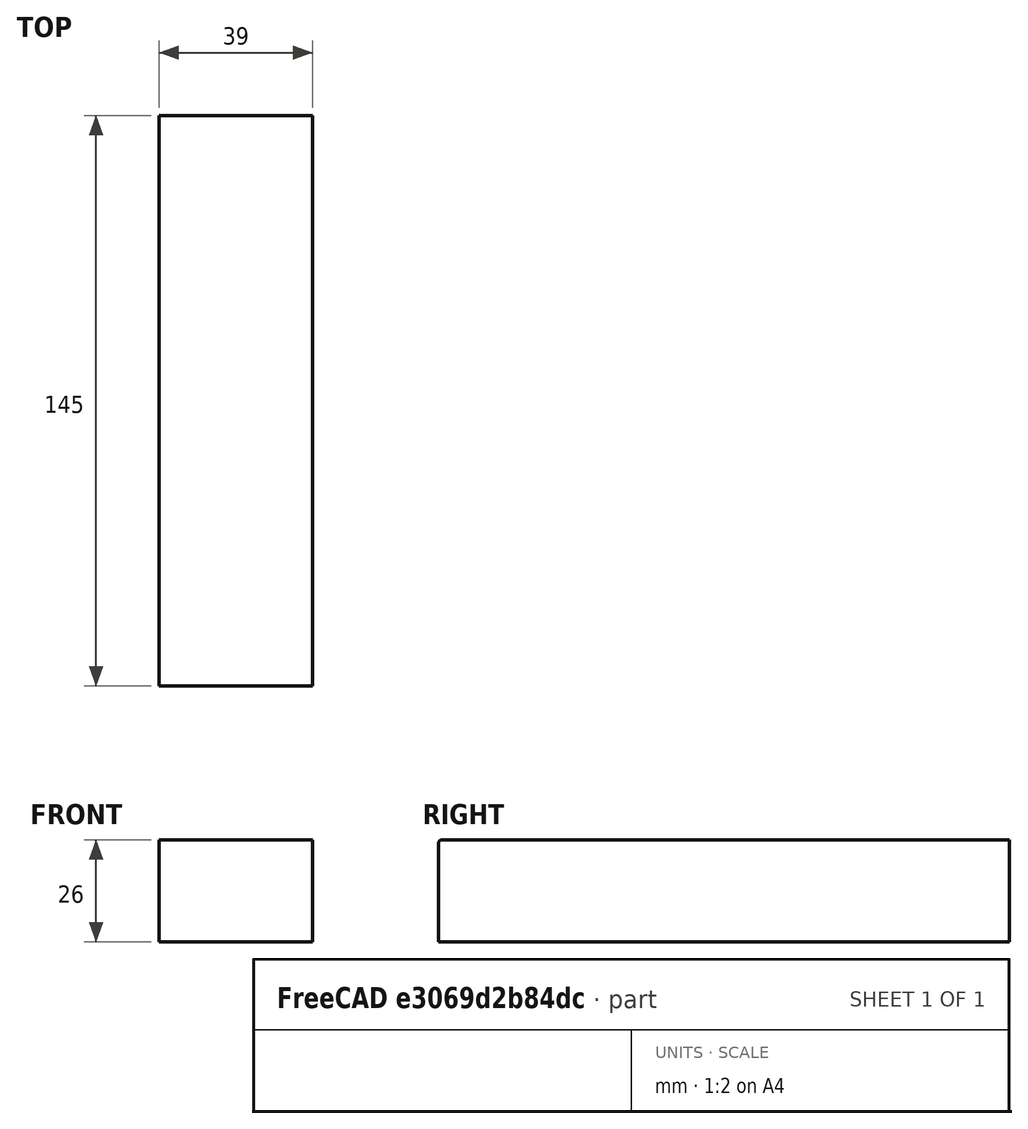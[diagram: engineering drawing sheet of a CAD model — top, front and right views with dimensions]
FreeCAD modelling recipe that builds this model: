
FCSTD DOCUMENT  (FreeCAD 0.17R13522 (Git))
Label: BlocLateralDroitClavier
License: All rights reserved
LicenseURL: http://en.wikipedia.org/wiki/All_rights_reserved
objects: Drawing::FeatureViewPython×6, Drawing::FeatureViewPart×3, Part::Box×1, Part::Fillet×1, Drawing::FeaturePage×1
note: 2 computed .brp shape members not serialized (recipe doc carries the construction recipe); baked Part::Feature solids carry a one-line shape summary decoded from their .brp

FEATURE [Part::Box] Box  label="Cube"
  AttacherType = Attacher::AttachEngine3D
  Height = 26
  Length = 39
  Width = 145
FEATURE [Part::Fillet] Fillet
  Base = -> Box
  Edges = 1 edges r=1: [Edge10]
FEATURE [Drawing::FeatureViewPart] Ortho  label="Ortho_0_0"
  Direction = (0,0,1)
  HiddenWidth = 0.15
  LineWidth = 0.35
  Rotation = 90
  ShowHiddenLines = false
  ShowSmoothLines = true
  Source = -> Fillet
  Tolerance = 0.05
  ViewResult = <g id="Ortho_0_0"\n   transform="rotate(90,108,37.6667) translate(108,37.6667) scale(1,1)"\n  >\n<g   fill="none"\n   stroke="rgb(0, 0, 0)"\n   stroke-linecap="butt"\n   stroke-linejoin="miter"\n   stroke-width="0.350000"\n   transform="scale(1,-1)"\n  >\n<path d="M0,-2.22045e-16 C0,0.00209593 0,0.00419186 0,0.00628779  C0,0.0125492 0,0.0188107 0,0.0250721  C0,0.0354203 0,0.0457685 0,0.0561167  C0,0.0704215 0,0.0847263 0,0.0990311  C0,0.117113 0,0.135194 0,0.153276  C0,0.174907 0,0.196538 0,0.218169  C0,0.243077 0,0.267985 0,0.292893  C0,0.320766 0,0.348638 0,0.37651  C0,0.436231 0,0.499433 0,0.566116  C0,0.701837 0,0.850207 0,1 " /><path id= "2" d=" M 0 1 L 0 145 " />\n<path id= "3" d=" M 0 -2.22045e-16 L 39 -2.22045e-16 " />\n<path d="M39,-2.22045e-16 C39,0.00209593 39,0.00419186 39,0.00628779  C39,0.0125492 39,0.0188107 39,0.0250721  C39,0.0354203 39,0.0457685 39,0.0561167  C39,0.0704215 39,0.0847263 39,0.0990311  C39,0.117113 39,0.135194 39,0.153276  C39,0.174907 39,0.196538 39,0.218169  C39,0.243077 39,0.267985 39,0.292893  C39,0.320766 39,0.348638 39,0.37651  C39,0.436231 39,0.499433 39,0.566116  C39,0.701837 39,0.850207 39,1 " /><path id= "5" d=" M 0 145 L 39 145 " />\n<path id= "6" d=" M 39 1 L 39 145 " />\n</g>\n<g   fill="none"\n   stroke="rgb(0, 0, 0)"\n   stroke-linecap="butt"\n   stroke-linejoin="miter"\n   stroke-width="0.350000"\n   transform="scale(1,-1)"\n  >\n<path id= "1" d=" M 0 1 L 39 1 " />\n</g>\n</g>
  Visible = false
  X = 108
  Y = 37.6667
FEATURE [Drawing::FeatureViewPart] Ortho001  label="Ortho_-1_0"
  Direction = (0,1,0)
  HiddenWidth = 0.15
  LineWidth = 0.35
  Rotation = 180
  ShowHiddenLines = false
  ShowSmoothLines = true
  Source = -> Fillet
  Tolerance = 0.05
  ViewResult = <g id="Ortho_-1_0"\n   transform="rotate(180,74,37.6667) translate(74,37.6667) scale(1,1)"\n  >\n<g   fill="none"\n   stroke="rgb(0, 0, 0)"\n   stroke-linecap="butt"\n   stroke-linejoin="miter"\n   stroke-width="0.350000"\n   transform="scale(1,-1)"\n  >\n<path id= "1" d=" M 0 0 L 26 0 " />\n<path id= "2" d=" M 0 0 L 0 39 " />\n<path id= "3" d=" M 26 0 L 26 39 " />\n<path id= "4" d=" M 0 39 L 26 39 " />\n</g>\n</g>
  Visible = false
  X = 74
  Y = 37.6667
FEATURE [Drawing::FeatureViewPart] Ortho002  label="Ortho_0_-1"
  Direction = (-1,0,0)
  HiddenWidth = 0.15
  LineWidth = 0.35
  Rotation = -90
  ShowHiddenLines = false
  ShowSmoothLines = true
  Source = -> Fillet
  Tolerance = 0.05
  ViewResult = <g id="Ortho_0_-1"\n   transform="rotate(-90,108,104.333) translate(108,104.333) scale(1,1)"\n  >\n<g   fill="none"\n   stroke="rgb(0, 0, 0)"\n   stroke-linecap="butt"\n   stroke-linejoin="miter"\n   stroke-width="0.350000"\n   transform="scale(1,-1)"\n  >\n<path id= "1" d=" M 0 0 L -25 0 " />\n<path d="M-25 2.22045e-16 A1 1 0 0 1 -26 -1" /><path id= "3" d=" M 0 0 L 0 -145 " />\n<path id= "4" d=" M -26 -1 L -26 -145 " />\n<path id= "5" d=" M 0 -145 L -26 -145 " />\n</g>\n</g>
  Visible = false
  X = 108
  Y = 104.333
FEATURE [Drawing::FeatureViewPython] dim001  # drawing view (typed FeaturePython)
  Rotation = 0
  ViewResult = <g> \n  <line x1="74.000000" y1="35.666700" x2="74.000000" y2="24.000000" style="stroke:rgb(0,0,255);stroke-width:0.30" />\n<line x1="48.000000" y1="35.666700" x2="48.000000" y2="24.000000" style="stroke:rgb(0,0,255);stroke-width:0.30" />\n<line x1="74.000000" y1="25.000000" x2="48.000000" y2="25.000000" style="stroke:rgb(0,0,255);stroke-width:0.30" /> \n  <polygon points="48.000000,25.000000 51.000000,26.000000 52.000000,25.000000 51.000000,24.000000" style="fill:rgb(0,0,255);stroke:rgb(0,0,255);stroke-width:0" /><polygon points="74.000000,25.000000 71.000000,24.000000 70.000000,25.000000 71.000000,26.000000" style="fill:rgb(0,0,255);stroke:rgb(0,0,255);stroke-width:0" /> \n  <text x="61.000000" y="23.000000" font-family="Verdana" font-size="3.6" fill="rgb(0,0,255)" text-anchor="middle" transform="rotate(0.000000 61.000000,23.000000)" > 26</text> </g>
  Visible = false
  X = 0
  Y = 0
  arrowL1 = 3
  arrowL2 = 1
  arrowW = 2
  arrow_scheme = 0
  autoPlaceOffset = 2
  autoPlaceText = true
  click1_x = 61.8667
  click1_y = 25
  click2_x = 61.8667
  click2_y = 25
  comma_decimal_place = false
  dimension_line_overshoot = 1
  gap_datum_points = 2
  halfDimension_linear = false
  lineColor = rgb(0,0,255)
  strokeWidth = 0.3
  textFormat_linear = %(value)3.0f
  textRenderer_color = rgb(0,0,255)
  textRenderer_family = Verdana
  textRenderer_size = 3.6
  unit_custom_scale = 1
  unit_scheme = 0
FEATURE [Drawing::FeatureViewPython] dim002  # drawing view (typed FeaturePython)
  Rotation = 0
  ViewResult = <g> \n  <line x1="46.000000" y1="37.666700" x2="30.533333" y2="37.666700" style="stroke:rgb(0,0,255);stroke-width:0.30" />\n<line x1="46.000000" y1="76.666700" x2="30.533333" y2="76.666700" style="stroke:rgb(0,0,255);stroke-width:0.30" />\n<line x1="31.533333" y1="37.666700" x2="31.533333" y2="76.666700" style="stroke:rgb(0,0,255);stroke-width:0.30" /> \n  <polygon points="31.533333,76.666700 32.533333,73.666700 31.533333,72.666700 30.533333,73.666700" style="fill:rgb(0,0,255);stroke:rgb(0,0,255);stroke-width:0" /><polygon points="31.533333,37.666700 30.533333,40.666700 31.533333,41.666700 32.533333,40.666700" style="fill:rgb(0,0,255);stroke:rgb(0,0,255);stroke-width:0" /> \n  <text x="29.533333" y="57.166700" font-family="Verdana" font-size="3.6" fill="rgb(0,0,255)" text-anchor="middle" transform="rotate(-90.000000 29.533333,57.166700)" > 39</text> </g>
  Visible = false
  X = 0
  Y = 0
  arrowL1 = 3
  arrowL2 = 1
  arrowW = 2
  arrow_scheme = 0
  autoPlaceOffset = 2
  autoPlaceText = true
  click1_x = 31.5333
  click1_y = 50
  click2_x = 31.5333
  click2_y = 50
  comma_decimal_place = false
  dimension_line_overshoot = 1
  gap_datum_points = 2
  halfDimension_linear = false
  lineColor = rgb(0,0,255)
  strokeWidth = 0.3
  textFormat_linear = %(value)3.0f
  textRenderer_color = rgb(0,0,255)
  textRenderer_family = Verdana
  textRenderer_size = 3.6
  unit_custom_scale = 1
  unit_scheme = 0
FEATURE [Drawing::FeatureViewPython] dim003  # drawing view (typed FeaturePython)
  Rotation = 0
  ViewResult = <g> \n  <line x1="108.099031" y1="78.666700" x2="108.099031" y2="86.000000" style="stroke:rgb(0,0,255);stroke-width:0.30" />\n<line x1="253.000000" y1="78.666700" x2="253.000000" y2="86.000000" style="stroke:rgb(0,0,255);stroke-width:0.30" />\n<line x1="108.099031" y1="85.000000" x2="253.000000" y2="85.000000" style="stroke:rgb(0,0,255);stroke-width:0.30" /> \n  <polygon points="253.000000,85.000000 250.000000,84.000000 249.000000,85.000000 250.000000,86.000000" style="fill:rgb(0,0,255);stroke:rgb(0,0,255);stroke-width:0" /><polygon points="108.099031,85.000000 111.099031,86.000000 112.099031,85.000000 111.099031,84.000000" style="fill:rgb(0,0,255);stroke:rgb(0,0,255);stroke-width:0" /> \n  <text x="180.549516" y="83.000000" font-family="Verdana" font-size="3.6" fill="rgb(0,0,255)" text-anchor="middle" transform="rotate(0.000000 180.549516,83.000000)" >145</text> </g>
  Visible = false
  X = 0
  Y = 0
  arrowL1 = 3
  arrowL2 = 1
  arrowW = 2
  arrow_scheme = 0
  autoPlaceOffset = 2
  autoPlaceText = true
  click1_x = 250
  click1_y = 85
  click2_x = 250
  click2_y = 85
  comma_decimal_place = false
  dimension_line_overshoot = 1
  gap_datum_points = 2
  halfDimension_linear = false
  lineColor = rgb(0,0,255)
  strokeWidth = 0.3
  textFormat_linear = %(value)3.0f
  textRenderer_color = rgb(0,0,255)
  textRenderer_family = Verdana
  textRenderer_size = 3.6
  unit_custom_scale = 1
  unit_scheme = 0
FEATURE [Drawing::FeatureViewPython] dim004  # drawing view (typed FeaturePython)
  Rotation = 0
  ViewResult = <g> \n  <line x1="255.000000" y1="104.333000" x2="271.000000" y2="104.333000" style="stroke:rgb(0,0,255);stroke-width:0.30" />\n<line x1="255.000000" y1="130.333000" x2="271.000000" y2="130.333000" style="stroke:rgb(0,0,255);stroke-width:0.30" />\n<line x1="270.000000" y1="104.333000" x2="270.000000" y2="130.333000" style="stroke:rgb(0,0,255);stroke-width:0.30" /> \n  <polygon points="270.000000,130.333000 271.000000,127.333000 270.000000,126.333000 269.000000,127.333000" style="fill:rgb(0,0,255);stroke:rgb(0,0,255);stroke-width:0" /><polygon points="270.000000,104.333000 269.000000,107.333000 270.000000,108.333000 271.000000,107.333000" style="fill:rgb(0,0,255);stroke:rgb(0,0,255);stroke-width:0" /> \n  <text x="268.000000" y="117.333000" font-family="Verdana" font-size="3.6" fill="rgb(0,0,255)" text-anchor="middle" transform="rotate(-90.000000 268.000000,117.333000)" > 26</text> </g>
  Visible = false
  X = 0
  Y = 0
  arrowL1 = 3
  arrowL2 = 1
  arrowW = 2
  arrow_scheme = 0
  autoPlaceOffset = 2
  autoPlaceText = true
  click1_x = 270
  click1_y = 113.578
  click2_x = 270
  click2_y = 113.578
  comma_decimal_place = false
  dimension_line_overshoot = 1
  gap_datum_points = 2
  halfDimension_linear = false
  lineColor = rgb(0,0,255)
  strokeWidth = 0.3
  textFormat_linear = %(value)3.0f
  textRenderer_color = rgb(0,0,255)
  textRenderer_family = Verdana
  textRenderer_size = 3.6
  unit_custom_scale = 1
  unit_scheme = 0
FEATURE [Drawing::FeatureViewPython] dim005  # drawing view (typed FeaturePython)
  Rotation = 0
  ViewResult = <g> \n  <line x1="255.000000" y1="37.666700" x2="271.000000" y2="37.666700" style="stroke:rgb(0,0,255);stroke-width:0.30" />\n<line x1="255.000000" y1="76.666700" x2="271.000000" y2="76.666700" style="stroke:rgb(0,0,255);stroke-width:0.30" />\n<line x1="270.000000" y1="37.666700" x2="270.000000" y2="76.666700" style="stroke:rgb(0,0,255);stroke-width:0.30" /> \n  <polygon points="270.000000,76.666700 271.000000,73.666700 270.000000,72.666700 269.000000,73.666700" style="fill:rgb(0,0,255);stroke:rgb(0,0,255);stroke-width:0" /><polygon points="270.000000,37.666700 269.000000,40.666700 270.000000,41.666700 271.000000,40.666700" style="fill:rgb(0,0,255);stroke:rgb(0,0,255);stroke-width:0" /> \n  <text x="268.000000" y="57.166700" font-family="Verdana" font-size="3.6" fill="rgb(0,0,255)" text-anchor="middle" transform="rotate(-90.000000 268.000000,57.166700)" > 39</text> </g>
  Visible = false
  X = 0
  Y = 0
  arrowL1 = 3
  arrowL2 = 1
  arrowW = 2
  arrow_scheme = 0
  autoPlaceOffset = 2
  autoPlaceText = true
  click1_x = 270
  click1_y = 50
  click2_x = 270
  click2_y = 50
  comma_decimal_place = false
  dimension_line_overshoot = 1
  gap_datum_points = 2
  halfDimension_linear = false
  lineColor = rgb(0,0,255)
  strokeWidth = 0.3
  textFormat_linear = %(value)3.0f
  textRenderer_color = rgb(0,0,255)
  textRenderer_family = Verdana
  textRenderer_size = 3.6
  unit_custom_scale = 1
  unit_scheme = 0
FEATURE [Drawing::FeatureViewPython] noteCircle001  # drawing view (typed FeaturePython)
  Rotation = 0
  ViewResult = <g> <line x1="120.000000" y1="65.000000" x2="109.000000" y2="57.166700" style="stroke:rgb(0,0,255);stroke-width:0.30" />\n<line x1="120.000000" y1="65.000000" x2="130.000000" y2="65.000000" style="stroke:rgb(0,0,255);stroke-width:0.30" />\n <circle cx ="130.000000" cy ="65.000000" r="4.500000" stroke="rgb(0,0,255)" fill="rgb(255,255,255)" /> \n<text x="128.500000" y="66.500000" font-family="inherit" font-size="5" fill="rgb(0,150,0)" text-anchor="inherit"  >1</text> </g>
  Visible = false
  X = 0
  Y = 0
  click1_x = 120
  click1_y = 65
  click2_x = 130
  click2_y = 65
  lineColor = rgb(0,0,255)
  noteCircle_fill = rgb(255,255,255)
  noteCircle_radius = 4.5
  noteText = 1
  strokeWidth = 0.3
  textRenderer_noteCircle_color = rgb(0,150,0)
  textRenderer_noteCircle_family = inherit
  textRenderer_noteCircle_size = 5
FEATURE [Drawing::FeaturePage] Page
  EditableTexts = GB | Bloc droit clavier | 1: congé 1mm | pièce en 2 exemplaires | A4 | X / Y | 1 | PN | DN | DD/MM/YYYY | REV A
  Group = -> [Ortho,Ortho001,Ortho002,dim001,dim002,dim003,dim004,dim005,noteCircle001]
  Template = <path>
note: 1 file-system path scrubbed to <path> (originals preserved in the JSON sidecar)
